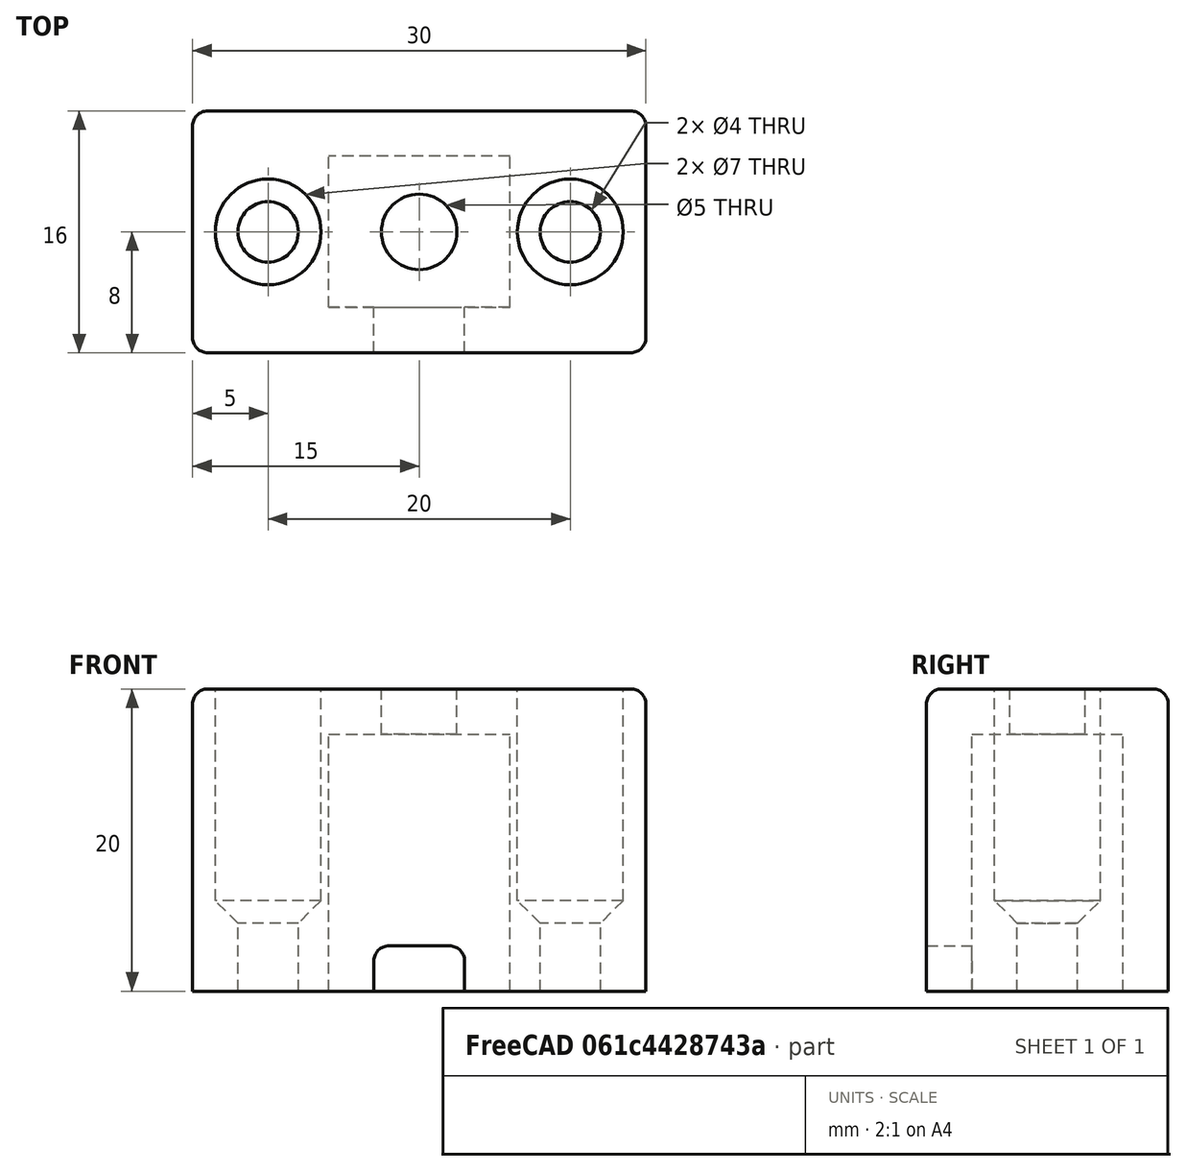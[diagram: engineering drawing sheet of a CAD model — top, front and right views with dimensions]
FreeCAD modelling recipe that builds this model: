
FCSTD DOCUMENT  (FreeCAD 0.19R24291 (Git))
Label: thermistor-selector
License: Other
LicenseURL: https://www.gnu.org/licenses/gpl-3.0.en.html
objects: Part::Cylinder×5, Part::Box×3, Part::Cut×3, Part::Chamfer×2, Part::Fillet×2, Part::MultiFuse×1
note: 16 computed .brp shape members not serialized (recipe doc carries the construction recipe); baked Part::Feature solids carry a one-line shape summary decoded from their .brp

FEATURE [Part::Box] Box  label="Cube"
  AttacherType = Attacher::AttachEngine3D
  Height = 20
  Length = 30
  Width = 16
FEATURE [Part::Box] Box001  label="Cube001"
  AttacherType = Attacher::AttachEngine3D
  Height = 20
  Length = 12
  Placement = pos=(9,3,-3) rot=(0,0,1;0rad)
  Width = 10
FEATURE [Part::Cylinder] Cylinder
  Angle = 360
  AttacherType = Attacher::AttachEngine3D
  Height = 33
  Placement = pos=(5,8,-1) rot=(0,0,1;0rad)
  Radius = 3.5
FEATURE [Part::Cylinder] Cylinder001
  Angle = 360
  AttacherType = Attacher::AttachEngine3D
  Height = 33
  Placement = pos=(25,8,-1) rot=(0,0,1;0rad)
  Radius = 3.5
FEATURE [Part::Chamfer] Chamfer
  Base = -> Cylinder
  Edges = 1 edges r=3: [Edge3]
  Placement = pos=(0,0,4) rot=(0,0,1;0rad)
FEATURE [Part::Chamfer] Chamfer001
  Base = -> Cylinder001
  Edges = 1 edges r=3: [Edge3]
  Placement = pos=(0,0,4) rot=(0,0,1;0rad)
FEATURE [Part::Cylinder] Cylinder002
  Angle = 360
  AttacherType = Attacher::AttachEngine3D
  Height = 33
  Placement = pos=(5,8,-1) rot=(0,0,1;0rad)
  Radius = 2
FEATURE [Part::Cylinder] Cylinder003
  Angle = 360
  AttacherType = Attacher::AttachEngine3D
  Height = 33
  Placement = pos=(25,8,-1) rot=(0,0,1;0rad)
  Radius = 2
FEATURE [Part::MultiFuse] Fusion  label="holes"
  Shapes = -> [Box001,Chamfer,Chamfer001,Cylinder002,Cylinder003]
FEATURE [Part::Cut] Cut
  Base = -> Box
  Tool = -> Fusion
FEATURE [Part::Cylinder] Cylinder004
  Angle = 360
  AttacherType = Attacher::AttachEngine3D
  Height = 10
  Placement = pos=(15,8,15) rot=(0,0,1;0rad)
  Radius = 2.5
FEATURE [Part::Cut] Cut001
  Base = -> Cut
  Tool = -> Cylinder004
FEATURE [Part::Box] Box002  label="Cube002"
  AttacherType = Attacher::AttachEngine3D
  Height = 4
  Length = 6
  Placement = pos=(12,-4,-1) rot=(0,0,1;0rad)
  Width = 10
FEATURE [Part::Cut] Cut002
  Base = -> Cut001
  Tool = -> Box002
FEATURE [Part::Fillet] Fillet
  Base = -> Cut002
  Edges = 2 edges r=1: [Edge29,Edge32]
FEATURE [Part::Fillet] Fillet001
  Base = -> Fillet
  Edges = 8 edges r=1: [Edge3,Edge4,Edge5,Edge29,Edge30,Edge33,Edge34,Edge39]
